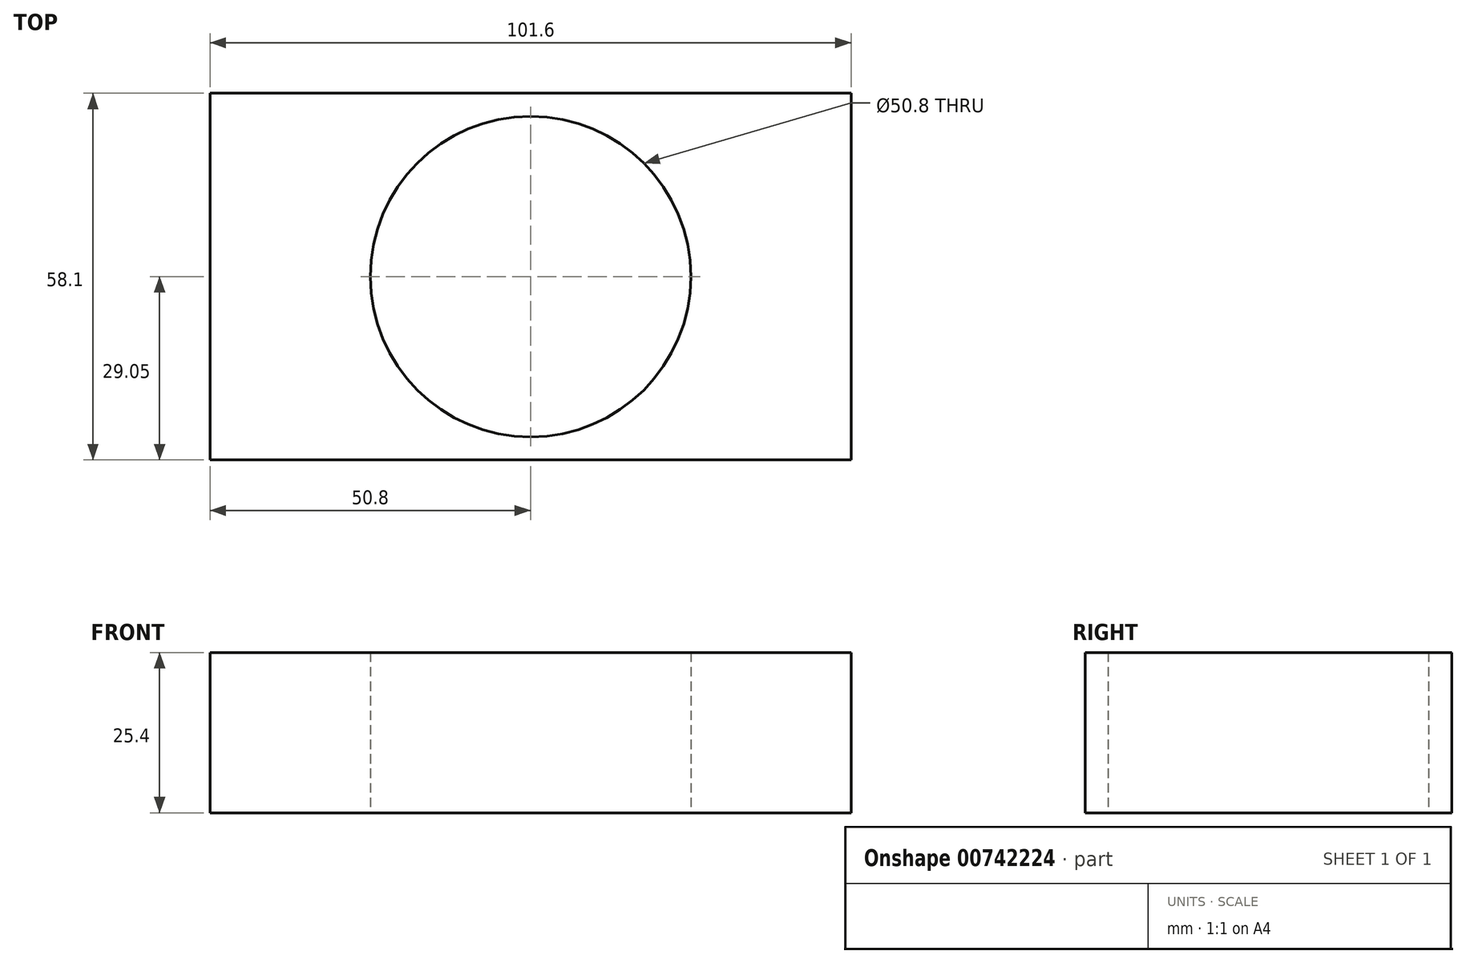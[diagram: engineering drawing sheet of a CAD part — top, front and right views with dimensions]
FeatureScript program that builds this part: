
annotation { "Feature Type Name" : "Feature", "Feature Type Description" : "" }
export const myFeature = defineFeature(function(context is Context, id is Id, definition is map)
    precondition{}
    {
        {
            var Q0;
            Q0=qCreatedBy(makeId("Top.planeOp"),FACE);
            var sketch = newSketch(context, id + "F0", { "sketchPlane" : qUnion([Q0])});
            skLineSegment(sketch, "E0.bottom", {"start": v(50.8, 29.05) * mm, "end": v(-50.8, 29.05) * mm});
            skLineSegment(sketch, "E0.top", {"start": v(50.8, -29.05) * mm, "end": v(-50.8, -29.05) * mm});
            skLineSegment(sketch, "E0.left", {"start": v(50.8, 29.05) * mm, "end": v(50.8, -29.05) * mm});
            skLineSegment(sketch, "E0.right", {"start": v(-50.8, 29.05) * mm, "end": v(-50.8, -29.05) * mm});
            skPoint(sketch, "E0.middle", {"position": v(0, 0) * mm});
            skCircle(sketch, "E1", {"center": v(0, 0) * mm, "radius": 25.4 * mm});
            skSolve(sketch);
        }
        {
            var Q0;
            Q0=makeQuery(id+"F0.imprint","IMPRINT",FACE,{"disambiguationData":[TD([[makeQuery(id+"F0.imprint","IMPRINT",EDGE,{"derivedFrom":sQuery(id+"F0.wireOp",EDGE,"E0.bottom")}),1.0]])]});
            extrude(context, id + "F1", {"entities" : qUnion([Q0]), "endBound" : BoundingType.SYMMETRIC, "depth" : 25.4 * mm, "offsetDistance" : 25.4 * mm});
        }
    });
